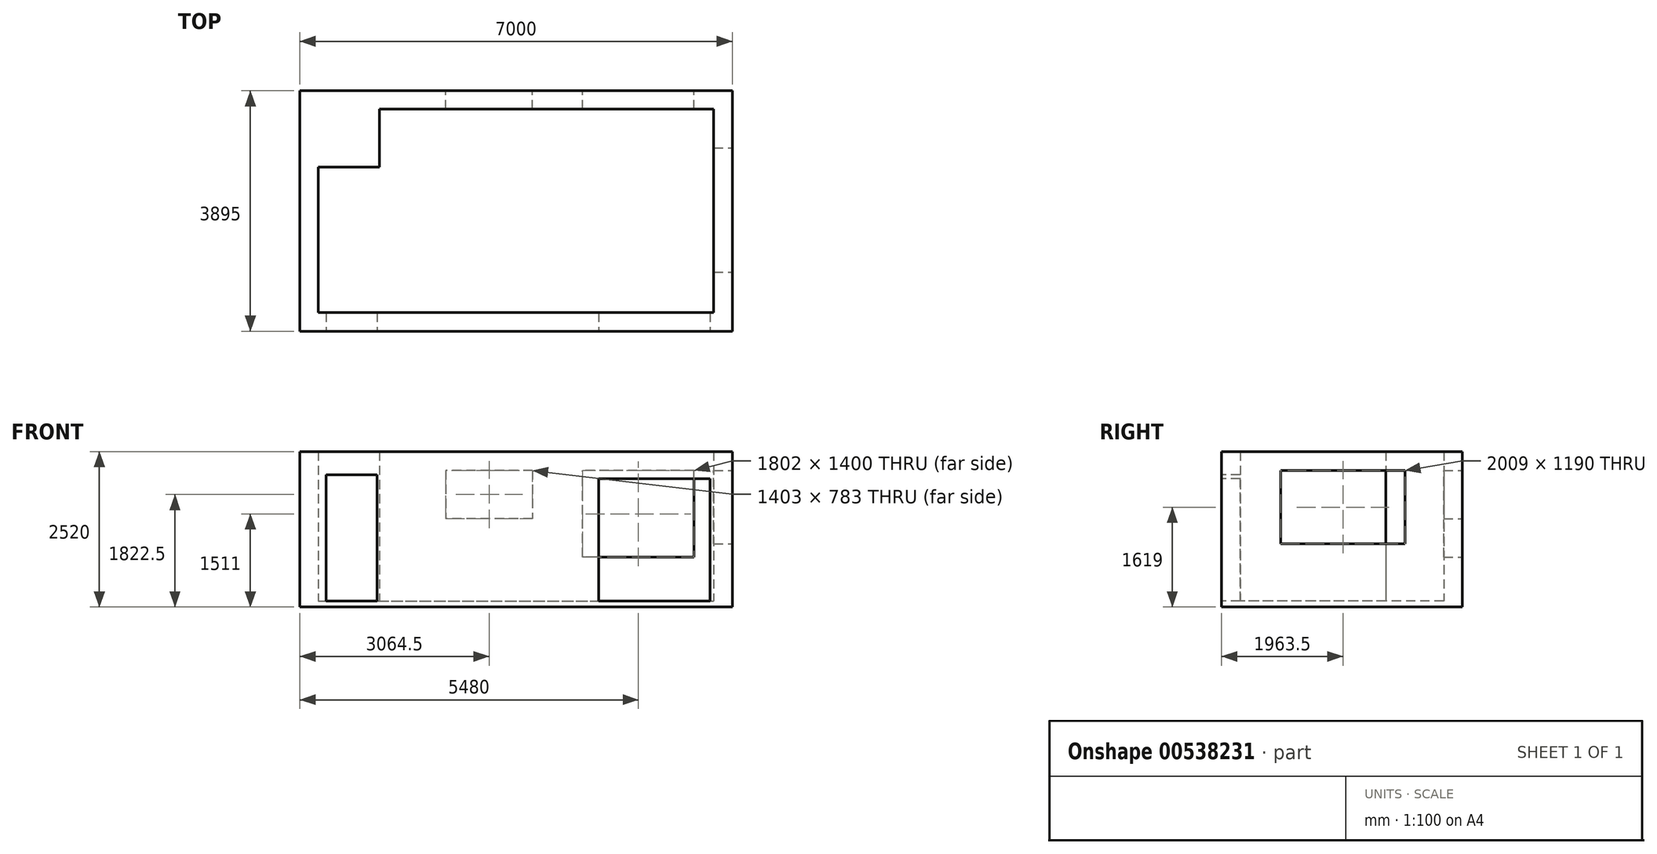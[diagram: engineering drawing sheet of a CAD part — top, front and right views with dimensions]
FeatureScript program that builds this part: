
annotation { "Feature Type Name" : "Feature", "Feature Type Description" : "" }
export const myFeature = defineFeature(function(context is Context, id is Id, definition is map)
    precondition{}
    {
        {
            var Q0;
            Q0=qCreatedBy(makeId("Top.planeOp"),FACE);
            var sketch = newSketch(context, id + "F0", { "sketchPlane" : qUnion([Q0])});
            skLineSegment(sketch, "E0.bottom", {"start": v(0, 0) * mm, "end": v(6400, 0) * mm});
            skLineSegment(sketch, "E0.top", {"start": v(0, -3295) * mm, "end": v(6400, -3295) * mm});
            skLineSegment(sketch, "E0.left", {"start": v(0, 0) * mm, "end": v(0, -3295) * mm});
            skLineSegment(sketch, "E0.right", {"start": v(6400, 0) * mm, "end": v(6400, -3295) * mm});
            skLineSegment(sketch, "E1", {"start": v(-300, 300) * mm, "end": v(-300, -3595) * mm});
            skLineSegment(sketch, "E2", {"start": v(-300, -3595) * mm, "end": v(6700, -3595) * mm});
            skLineSegment(sketch, "E3", {"start": v(-300, 300) * mm, "end": v(6700, 300) * mm});
            skLineSegment(sketch, "E4", {"start": v(6700, 300) * mm, "end": v(6700, -3595) * mm});
            skSolve(sketch);
        }
        {
            var Q0;
            Q0=makeQuery(id+"F0.imprint","IMPRINT",FACE,{"disambiguationData":[TD([[makeQuery(id+"F0.imprint","IMPRINT",EDGE,{"derivedFrom":sQuery(id+"F0.wireOp",EDGE,"E0.bottom")}),1.0]])]});
            extrude(context, id + "F1", {"entities" : qUnion([Q0]), "depth" : 2420 * mm, "offsetDistance" : 25 * mm});
        }
        {
            var Q0;
            Q0=makeQuery(id+"F1.opExtrude","SWEPT_FACE",FACE,{"disambiguationData":[OSD([sQuery(id+"F0.wireOp",EDGE,"E2")])]});
            var sketch = newSketch(context, id + "F2", { "sketchPlane" : qUnion([Q0])});
            skLineSegment(sketch, "E5.bottom", {"start": v(6340, 0) * mm, "end": v(4539, 0) * mm});
            skLineSegment(sketch, "E5.top", {"start": v(6340, 1982) * mm, "end": v(4539, 1982) * mm});
            skLineSegment(sketch, "E5.left", {"start": v(6340, 0) * mm, "end": v(6340, 1982) * mm});
            skLineSegment(sketch, "E5.right", {"start": v(4539, 0) * mm, "end": v(4539, 1982) * mm});
            skSolve(sketch);
        }
        {
            var Q0;
            Q0 = qSketchRegion(id + "F2", true);
            extrude(context, id + "F3", {"entities" : qUnion([Q0]), "operationType" : NewBodyOperationType.REMOVE, "oppositeDirection" : true, "depth" : 300 * mm, "offsetDistance" : 25 * mm});
        }
        {
            var Q0;
            Q0=makeQuery(id+"F1.opExtrude","SWEPT_FACE",FACE,{"disambiguationData":[OSD([sQuery(id+"F0.wireOp",EDGE,"E2")])]});
            var sketch = newSketch(context, id + "F4", { "sketchPlane" : qUnion([Q0])});
            skLineSegment(sketch, "E6.bottom", {"start": v(121, 0) * mm, "end": v(948, 0) * mm});
            skLineSegment(sketch, "E6.top", {"start": v(121, 2044) * mm, "end": v(948, 2044) * mm});
            skLineSegment(sketch, "E6.left", {"start": v(121, 0) * mm, "end": v(121, 2044) * mm});
            skLineSegment(sketch, "E6.right", {"start": v(948, 0) * mm, "end": v(948, 2044) * mm});
            skSolve(sketch);
        }
        {
            var Q0;
            Q0 = qSketchRegion(id + "F4", true);
            extrude(context, id + "F5", {"entities" : qUnion([Q0]), "operationType" : NewBodyOperationType.REMOVE, "oppositeDirection" : true, "depth" : 300 * mm, "offsetDistance" : 25 * mm});
        }
        {
            var Q0;
            Q0=makeQuery(id+"F1.opExtrude","SWEPT_FACE",FACE,{"disambiguationData":[OSD([sQuery(id+"F0.wireOp",EDGE,"E4")])]});
            var sketch = newSketch(context, id + "F6", { "sketchPlane" : qUnion([Q0])});
            skLineSegment(sketch, "E7.bottom", {"start": v(-627, 924) * mm, "end": v(-2636, 924) * mm});
            skLineSegment(sketch, "E7.top", {"start": v(-627, 2114) * mm, "end": v(-2636, 2114) * mm});
            skLineSegment(sketch, "E7.left", {"start": v(-627, 924) * mm, "end": v(-627, 2114) * mm});
            skLineSegment(sketch, "E7.right", {"start": v(-2636, 924) * mm, "end": v(-2636, 2114) * mm});
            skSolve(sketch);
        }
        {
            var Q0;
            Q0 = qSketchRegion(id + "F6", true);
            extrude(context, id + "F7", {"entities" : qUnion([Q0]), "operationType" : NewBodyOperationType.REMOVE, "oppositeDirection" : true, "depth" : 300 * mm, "offsetDistance" : 25 * mm});
        }
        {
            var Q0;
            Q0=makeQuery(id+"F1.opExtrude","SWEPT_FACE",FACE,{"disambiguationData":[OSD([sQuery(id+"F0.wireOp",EDGE,"E3")])]});
            var sketch = newSketch(context, id + "F8", { "sketchPlane" : qUnion([Q0])});
            skLineSegment(sketch, "E8.bottom", {"start": v(-6081, 711) * mm, "end": v(-4279, 711) * mm});
            skLineSegment(sketch, "E8.top", {"start": v(-6081, 2111) * mm, "end": v(-4279, 2111) * mm});
            skLineSegment(sketch, "E8.left", {"start": v(-6081, 711) * mm, "end": v(-6081, 2111) * mm});
            skLineSegment(sketch, "E8.right", {"start": v(-4279, 711) * mm, "end": v(-4279, 2111) * mm});
            skSolve(sketch);
        }
        {
            var Q0;
            Q0 = qSketchRegion(id + "F8", true);
            extrude(context, id + "F9", {"entities" : qUnion([Q0]), "operationType" : NewBodyOperationType.REMOVE, "oppositeDirection" : true, "depth" : 300 * mm, "offsetDistance" : 25 * mm});
        }
        {
            var Q0;
            Q0=qCreatedBy(makeId("Top.planeOp"),FACE);
            var sketch = newSketch(context, id + "F10", { "sketchPlane" : qUnion([Q0])});
            skLineSegment(sketch, "E9.bottom", {"start": v(0, 0) * mm, "end": v(988, 0) * mm});
            skLineSegment(sketch, "E9.top", {"start": v(0, -939) * mm, "end": v(988, -939) * mm});
            skLineSegment(sketch, "E9.left", {"start": v(0, 0) * mm, "end": v(0, -939) * mm});
            skLineSegment(sketch, "E9.right", {"start": v(988, 0) * mm, "end": v(988, -939) * mm});
            skSolve(sketch);
        }
        {
            var Q0;
            Q0 = qSketchRegion(id + "F10", true);
            extrude(context, id + "F11", {"entities" : qUnion([Q0]), "operationType" : NewBodyOperationType.ADD, "depth" : 2420 * mm, "offsetDistance" : 25 * mm});
        }
        {
            var Q0;
            Q0=makeQuery(id+"F1.opExtrude","SWEPT_FACE",FACE,{"disambiguationData":[OSD([sQuery(id+"F0.wireOp",EDGE,"E3")])]});
            var sketch = newSketch(context, id + "F12", { "sketchPlane" : qUnion([Q0])});
            skLineSegment(sketch, "E10.bottom", {"start": v(-3466, 2114) * mm, "end": v(-2063, 2114) * mm});
            skLineSegment(sketch, "E10.top", {"start": v(-3466, 1331) * mm, "end": v(-2063, 1331) * mm});
            skLineSegment(sketch, "E10.left", {"start": v(-3466, 2114) * mm, "end": v(-3466, 1331) * mm});
            skLineSegment(sketch, "E10.right", {"start": v(-2063, 2114) * mm, "end": v(-2063, 1331) * mm});
            skSolve(sketch);
        }
        {
            var Q0;
            Q0 = qSketchRegion(id + "F12", true);
            extrude(context, id + "F13", {"entities" : qUnion([Q0]), "operationType" : NewBodyOperationType.REMOVE, "oppositeDirection" : true, "depth" : 300 * mm, "offsetDistance" : 25 * mm});
        }
        {
            var Q0;
            Q0=qCreatedBy(makeId("Top.planeOp"),FACE);
            var sketch = newSketch(context, id + "F14", { "sketchPlane" : qUnion([Q0])});
            skLineSegment(sketch, "E11.0", {"start": v(-300, 300) * mm, "end": v(-300, -3595) * mm});
            skLineSegment(sketch, "E12.0", {"start": v(6700, 300) * mm, "end": v(6700, -3595) * mm});
            skLineSegment(sketch, "E13", {"start": v(-300, -3595) * mm, "end": v(6700, -3595) * mm});
            skLineSegment(sketch, "E14", {"start": v(6700, 300) * mm, "end": v(-300, 300) * mm});
            skSolve(sketch);
        }
        {
            var Q0;
            Q0 = qSketchRegion(id + "F14", true);
            extrude(context, id + "F15", {"entities" : qUnion([Q0]), "operationType" : NewBodyOperationType.ADD, "oppositeDirection" : true, "depth" : 100 * mm, "offsetDistance" : 25 * mm});
        }
    });
